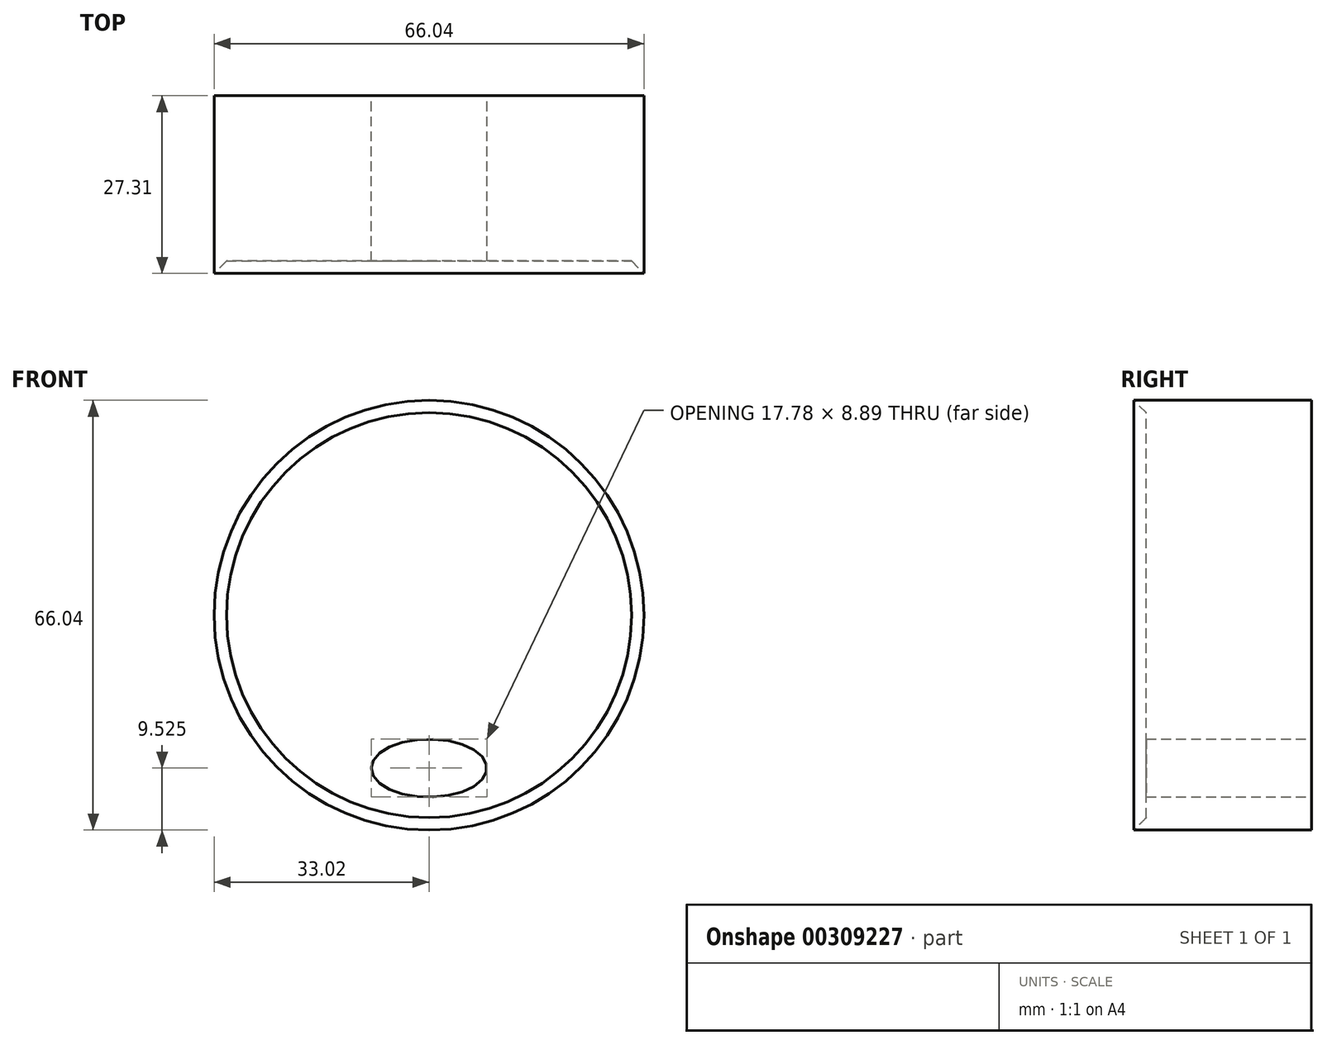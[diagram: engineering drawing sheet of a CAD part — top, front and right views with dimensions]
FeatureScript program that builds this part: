
annotation { "Feature Type Name" : "Feature", "Feature Type Description" : "" }
export const myFeature = defineFeature(function(context is Context, id is Id, definition is map)
    precondition{}
    {
        {
            var Q0;
            Q0=qCreatedBy(makeId("Front.planeOp"),FACE);
            var sketch = newSketch(context, id + "F0", { "sketchPlane" : qUnion([Q0])});
            skCircle(sketch, "E0", {"center": v(0, 0) * mm, "radius": 33.02 * mm});
            skEllipse(sketch, "E1", {"center": v(0, -23.5) * mm, "majorRadius": 8.9 * mm, "minorRadius": 4.45 * mm, "majorAxis": v(-1, 0)});
            skCircle(sketch, "E2", {"center": v(0, 0) * mm, "radius": 28.58 * mm});
            skSolve(sketch);
        }
        {
            var Q0;
            Q0=makeQuery(id+"F0.imprint","IMPRINT",FACE,{"disambiguationData":[TD([[makeQuery(id+"F0.imprint","IMPRINT",EDGE,{"derivedFrom":sQuery(id+"F0.wireOp",EDGE,"E0")}),1.0]])]});
            extrude(context, id + "F1", {"entities" : qUnion([Q0]), "depth" : 27.94 * mm});
        }
        {
            var Q0;
            Q0=makeQuery(id+"F0.imprint","IMPRINT",FACE,{"disambiguationData":[TD([[makeQuery(id+"F0.imprint","IMPRINT",EDGE,{"derivedFrom":sQuery(id+"F0.wireOp",EDGE,"E1")}),-1.0]])]});
            extrude(context, id + "F2", {"entities" : qUnion([Q0]), "operationType" : NewBodyOperationType.ADD, "depth" : 25.4 * mm});
        }
        {
            var Q0;
            Q0=makeQuery(id+"F1.opExtrude","CAP_EDGE",EDGE,{"disambiguationData":[OSD([sQuery(id+"F0.wireOp",EDGE,"E2")])],"isStart":false});
            chamfer(context, id + "F3", {"entities" : qUnion([Q0]), "width" : 5.08 * mm, "tangentPropagation" : true});
        }
    });
